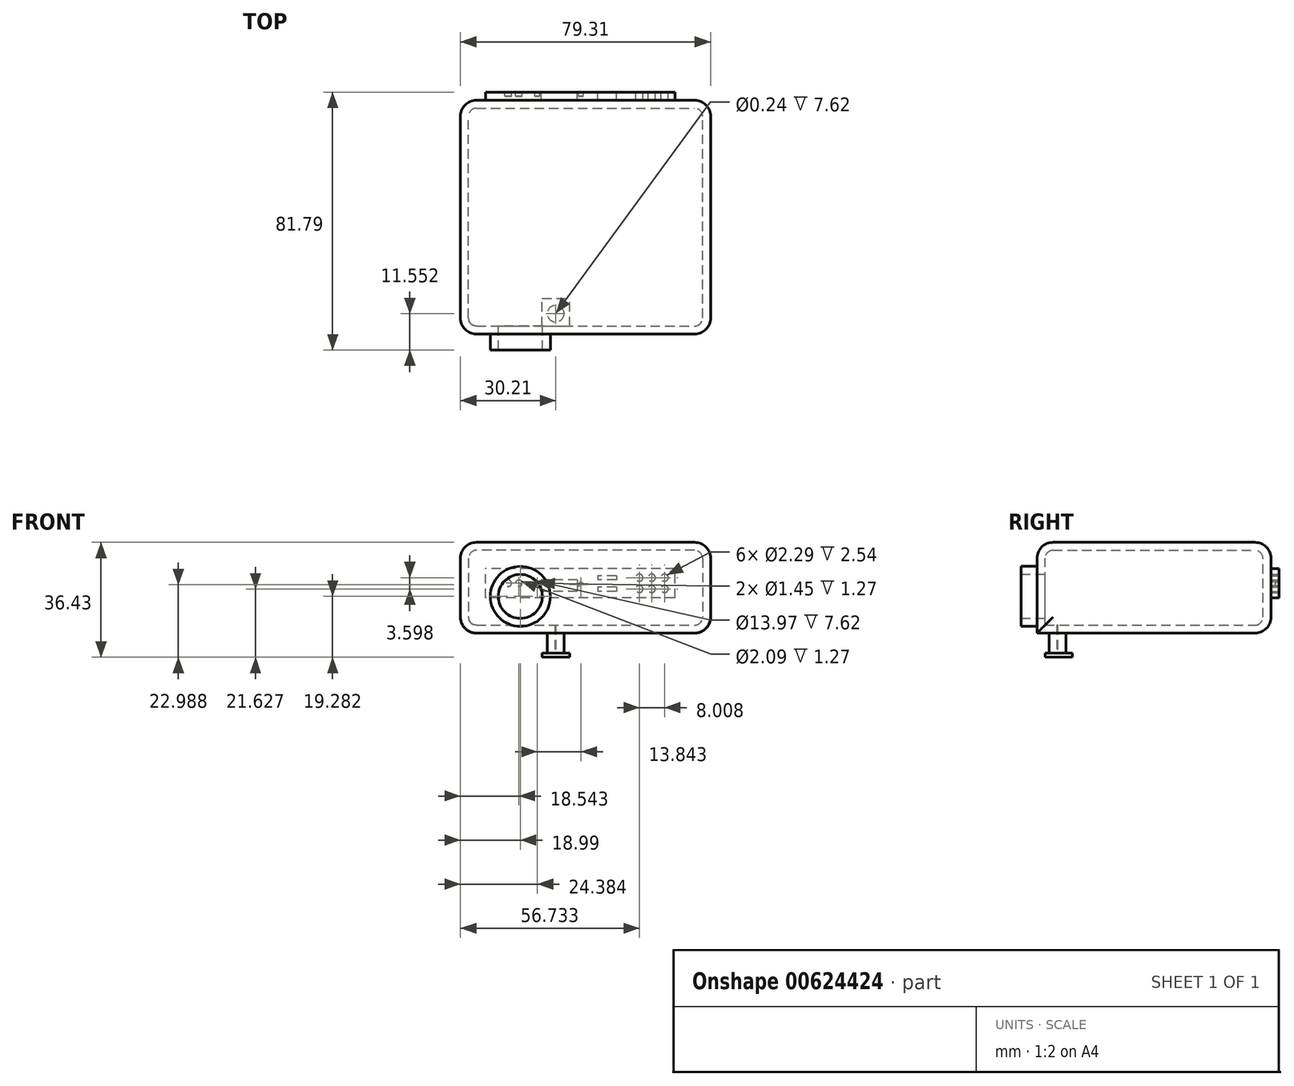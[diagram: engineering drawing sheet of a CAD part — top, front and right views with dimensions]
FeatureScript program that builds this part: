
annotation { "Feature Type Name" : "Feature", "Feature Type Description" : "" }
export const myFeature = defineFeature(function(context is Context, id is Id, definition is map)
    precondition{}
    {
        {
            var Q0;
            Q0=qCreatedBy(makeId("Front.planeOp"),FACE);
            var sketch = newSketch(context, id + "F0", { "sketchPlane" : qUnion([Q0])});
            skLineSegment(sketch, "E0.bottom", {"start": v(0, 0) * mm, "end": v(79.31, 0) * mm});
            skLineSegment(sketch, "E0.top", {"start": v(0, 28.8) * mm, "end": v(79.31, 28.8) * mm});
            skLineSegment(sketch, "E0.left", {"start": v(0, 0) * mm, "end": v(0, 28.8) * mm});
            skLineSegment(sketch, "E0.right", {"start": v(79.31, 0) * mm, "end": v(79.31, 28.8) * mm});
            skSolve(sketch);
        }
        {
            var Q0;
            Q0=makeQuery(id+"F0.imprint","IMPRINT",FACE,{"disambiguationData":[TD([[makeQuery(id+"F0.imprint","IMPRINT",EDGE,{"derivedFrom":sQuery(id+"F0.wireOp",EDGE,"E0.bottom")}),1.0]])]});
            extrude(context, id + "F1", {"entities" : qUnion([Q0]), "oppositeDirection" : true, "depth" : 74.17 * mm, "offsetDistance" : 25.4 * mm});
        }
        {
            var Q0;
            Q0=makeQuery(id+"F1.opExtrude","CAP_FACE",FACE,{"disambiguationData":[OSD([sQuery(id+"F0.wireOp",EDGE,"E0.bottom"),sQuery(id+"F0.wireOp",EDGE,"E0.top"),sQuery(id+"F0.wireOp",EDGE,"E0.left"),sQuery(id+"F0.wireOp",EDGE,"E0.right")])],"isStart":false});
            fillet(context, id + "F2", {"entities" : qUnion([Q0]), "radius" : 5.08 * mm, "tangentPropagation" : true, "allowEdgeOverflow" : false});
        }
        {
            var Q0;
            Q0=makeQuery(id+"F1.opExtrude","SWEPT_FACE",FACE,{"disambiguationData":[OSD([sQuery(id+"F0.wireOp",EDGE,"E0.right")])]});
            fillet(context, id + "F3", {"entities" : qUnion([Q0]), "radius" : 5.08 * mm, "tangentPropagation" : true, "allowEdgeOverflow" : false});
        }
        {
            var Q0;
            Q0=makeQuery(id+"F1.opExtrude","SWEPT_FACE",FACE,{"disambiguationData":[OSD([sQuery(id+"F0.wireOp",EDGE,"E0.bottom")])]});
            var sketch = newSketch(context, id + "F4", { "sketchPlane" : qUnion([Q0])});
            skCircle(sketch, "E1", {"center": v(30.2, -6.47) * mm, "radius": 2.66 * mm});
            skSolve(sketch);
        }
        {
            var Q0;
            Q0 = qSketchRegion(id + "F4", true);
            extrude(context, id + "F5", {"entities" : qUnion([Q0]), "operationType" : NewBodyOperationType.ADD, "depth" : 6.35 * mm, "offsetDistance" : 25.4 * mm});
        }
        {
            var Q0;
            Q0=makeQuery(id+"F5.opExtrude","CAP_FACE",FACE,{"disambiguationData":[OSD([sQuery(id+"F4.wireOp",EDGE,"E1")])],"isStart":false});
            var sketch = newSketch(context, id + "F6", { "sketchPlane" : qUnion([Q0])});
            skLineSegment(sketch, "E2.bottom", {"start": v(25.91, -2.52) * mm, "end": v(34.65, -2.52) * mm});
            skLineSegment(sketch, "E2.top", {"start": v(25.91, -11.26) * mm, "end": v(34.65, -11.26) * mm});
            skLineSegment(sketch, "E2.left", {"start": v(25.91, -2.52) * mm, "end": v(25.91, -11.26) * mm});
            skLineSegment(sketch, "E2.right", {"start": v(34.65, -2.52) * mm, "end": v(34.65, -11.26) * mm});
            skSolve(sketch);
        }
        {
            var Q0;
            Q0 = qSketchRegion(id + "F6", true);
            extrude(context, id + "F7", {"entities" : qUnion([Q0]), "operationType" : NewBodyOperationType.ADD, "depth" : 1.27 * mm, "offsetDistance" : 25.4 * mm});
        }
        {
            var Q0;
            Q0=makeQuery(id+"F1.opExtrude","SWEPT_FACE",FACE,{"disambiguationData":[OSD([sQuery(id+"F0.wireOp",EDGE,"E0.top")])]});
            fillet(context, id + "F8", {"entities" : qUnion([Q0]), "radius" : 5.08 * mm, "tangentPropagation" : true, "allowEdgeOverflow" : false});
        }
        {
            var Q0;
            Q0=makeQuery(id+"F1.opExtrude","SWEPT_FACE",FACE,{"disambiguationData":[OSD([sQuery(id+"F0.wireOp",EDGE,"E0.left")])]});
            fillet(context, id + "F9", {"entities" : qUnion([Q0]), "radius" : 5.08 * mm, "tangentPropagation" : true, "allowEdgeOverflow" : false});
        }
        {
            var Q0;
            Q0=qCreatedBy(makeId("Front.planeOp"),FACE);
            var sketch = newSketch(context, id + "F10", { "sketchPlane" : qUnion([Q0])});
            skCircle(sketch, "E3", {"center": v(18.99, 11.66) * mm, "radius": 9.53 * mm});
            skSolve(sketch);
        }
        {
            var Q0;
            Q0 = qSketchRegion(id + "F10", true);
            extrude(context, id + "F11", {"entities" : qUnion([Q0]), "operationType" : NewBodyOperationType.ADD, "depth" : 5.08 * mm, "offsetDistance" : 25.4 * mm});
        }
        {
            var Q0;
            Q0=makeQuery(id+"F11.opExtrude","CAP_FACE",FACE,{"disambiguationData":[OSD([sQuery(id+"F10.wireOp",EDGE,"E3")])],"isStart":false});
            shell(context, id + "F12", {"entities" : qUnion([Q0]), "thickness" : 2.54 * mm});
        }
        {
            var Q0;
            Q0=makeQuery(id+"F1.opExtrude","CAP_FACE",FACE,{"disambiguationData":[OSD([sQuery(id+"F0.wireOp",EDGE,"E0.bottom"),sQuery(id+"F0.wireOp",EDGE,"E0.top"),sQuery(id+"F0.wireOp",EDGE,"E0.left"),sQuery(id+"F0.wireOp",EDGE,"E0.right")])],"isStart":false});
            var sketch = newSketch(context, id + "F13", { "sketchPlane" : qUnion([Q0])});
            skLineSegment(sketch, "E4.bottom", {"start": v(-68.05, 11.14) * mm, "end": v(-7.92, 11.14) * mm});
            skLineSegment(sketch, "E4.top", {"start": v(-68.05, 20.48) * mm, "end": v(-7.92, 20.48) * mm});
            skLineSegment(sketch, "E4.left", {"start": v(-68.05, 11.14) * mm, "end": v(-68.05, 20.48) * mm});
            skLineSegment(sketch, "E4.right", {"start": v(-7.92, 11.14) * mm, "end": v(-7.92, 20.48) * mm});
            skSolve(sketch);
        }
        {
            var Q0;
            Q0=makeQuery(id+"F13.imprint","IMPRINT",FACE,{"disambiguationData":[TD([[makeQuery(id+"F13.imprint","IMPRINT",EDGE,{"derivedFrom":sQuery(id+"F13.wireOp",EDGE,"E4.bottom")}),1.0]])]});
            extrude(context, id + "F14", {"entities" : qUnion([Q0]), "operationType" : NewBodyOperationType.ADD, "depth" : 2.54 * mm, "offsetDistance" : 25.4 * mm});
        }
        {
            var Q0;
            Q0=makeQuery(id+"F14.opExtrude","CAP_FACE",FACE,{"disambiguationData":[OSD([sQuery(id+"F13.wireOp",EDGE,"E4.bottom"),sQuery(id+"F13.wireOp",EDGE,"E4.top"),sQuery(id+"F13.wireOp",EDGE,"E4.left"),sQuery(id+"F13.wireOp",EDGE,"E4.right")])],"isStart":false});
            var sketch = newSketch(context, id + "F15", { "sketchPlane" : qUnion([Q0])});
            skCircle(sketch, "E5", {"center": v(-64.74, 17.6) * mm, "radius": 1.14 * mm});
            skCircle(sketch, "E6", {"center": v(-60.68, 17.6) * mm, "radius": 1.14 * mm});
            skCircle(sketch, "E7", {"center": v(-56.73, 17.6) * mm, "radius": 1.14 * mm});
            skCircle(sketch, "E8", {"center": v(-64.74, 14) * mm, "radius": 1.14 * mm});
            skCircle(sketch, "E9", {"center": v(-60.68, 14) * mm, "radius": 1.14 * mm});
            skCircle(sketch, "E10", {"center": v(-56.73, 14) * mm, "radius": 1.14 * mm});
            skSolve(sketch);
        }
        {
            var Q0;
            Q0=makeQuery(id+"F15.imprint","IMPRINT",FACE,{"disambiguationData":[TD([[makeQuery(id+"F15.imprint","IMPRINT",EDGE,{"derivedFrom":sQuery(id+"F15.wireOp",EDGE,"E5")}),-1.0]])]});
            var sketch = newSketch(context, id + "F16", { "sketchPlane" : qUnion([Q0])});
            skLineSegment(sketch, "E11.bottom", {"start": v(-49.45, 18.24) * mm, "end": v(-43.59, 18.24) * mm});
            skLineSegment(sketch, "E11.top", {"start": v(-49.45, 16.86) * mm, "end": v(-43.59, 16.86) * mm});
            skLineSegment(sketch, "E11.left", {"start": v(-49.45, 18.24) * mm, "end": v(-49.45, 16.86) * mm});
            skLineSegment(sketch, "E11.right", {"start": v(-43.59, 18.24) * mm, "end": v(-43.59, 16.86) * mm});
            skLineSegment(sketch, "E12.bottom", {"start": v(-49.45, 14.62) * mm, "end": v(-43.59, 14.62) * mm});
            skLineSegment(sketch, "E12.top", {"start": v(-49.45, 13.25) * mm, "end": v(-43.59, 13.25) * mm});
            skLineSegment(sketch, "E12.left", {"start": v(-49.45, 14.62) * mm, "end": v(-49.45, 13.25) * mm});
            skLineSegment(sketch, "E12.right", {"start": v(-43.59, 14.62) * mm, "end": v(-43.59, 13.25) * mm});
            skLineSegment(sketch, "E13.bottom", {"start": v(-37.1, 16.86) * mm, "end": v(-25.63, 16.86) * mm});
            skLineSegment(sketch, "E13.top", {"start": v(-37.1, 13.25) * mm, "end": v(-25.63, 13.25) * mm});
            skLineSegment(sketch, "E13.left", {"start": v(-37.1, 16.86) * mm, "end": v(-37.1, 13.25) * mm});
            skLineSegment(sketch, "E13.right", {"start": v(-25.63, 16.86) * mm, "end": v(-25.63, 13.25) * mm});
            skSolve(sketch);
        }
        {
            var Q0;
            Q0=makeQuery(id+"F15.imprint","IMPRINT",FACE,{"disambiguationData":[TD([[makeQuery(id+"F15.imprint","IMPRINT",EDGE,{"derivedFrom":sQuery(id+"F15.wireOp",EDGE,"E5")}),-1.0]])]});
            var sketch = newSketch(context, id + "F17", { "sketchPlane" : qUnion([Q0])});
            skCircle(sketch, "E14", {"center": v(-24.38, 15.37) * mm, "radius": 0.73 * mm});
            skCircle(sketch, "E15", {"center": v(-38.23, 15.37) * mm, "radius": 0.73 * mm});
            skSolve(sketch);
        }
        {
            var Q0;
            Q0=makeQuery(id+"F15.imprint","IMPRINT",FACE,{"disambiguationData":[TD([[makeQuery(id+"F15.imprint","IMPRINT",EDGE,{"derivedFrom":sQuery(id+"F15.wireOp",EDGE,"E5")}),1.0]])]});
            var Q1;
            Q1=makeQuery(id+"F15.imprint","IMPRINT",FACE,{"disambiguationData":[TD([[makeQuery(id+"F15.imprint","IMPRINT",EDGE,{"derivedFrom":sQuery(id+"F15.wireOp",EDGE,"E6")}),1.0]])]});
            var Q2;
            Q2=makeQuery(id+"F15.imprint","IMPRINT",FACE,{"disambiguationData":[TD([[makeQuery(id+"F15.imprint","IMPRINT",EDGE,{"derivedFrom":sQuery(id+"F15.wireOp",EDGE,"E7")}),1.0]])]});
            var Q3;
            Q3=makeQuery(id+"F15.imprint","IMPRINT",FACE,{"disambiguationData":[TD([[makeQuery(id+"F15.imprint","IMPRINT",EDGE,{"derivedFrom":sQuery(id+"F15.wireOp",EDGE,"E10")}),1.0]])]});
            var Q4;
            Q4=makeQuery(id+"F15.imprint","IMPRINT",FACE,{"disambiguationData":[TD([[makeQuery(id+"F15.imprint","IMPRINT",EDGE,{"derivedFrom":sQuery(id+"F15.wireOp",EDGE,"E9")}),1.0]])]});
            var Q5;
            Q5=makeQuery(id+"F15.imprint","IMPRINT",FACE,{"disambiguationData":[TD([[makeQuery(id+"F15.imprint","IMPRINT",EDGE,{"derivedFrom":sQuery(id+"F15.wireOp",EDGE,"E8")}),1.0]])]});
            extrude(context, id + "F18", {"entities" : qUnion([Q0, Q1, Q2, Q3, Q4, Q5]), "operationType" : NewBodyOperationType.REMOVE, "oppositeDirection" : true, "depth" : 2.54 * mm, "offsetDistance" : 25.4 * mm});
        }
        {
            var Q0;
            Q0=makeQuery(id+"F17.imprint","IMPRINT",FACE,{"disambiguationData":[TD([[makeQuery(id+"F17.imprint","IMPRINT",EDGE,{"derivedFrom":sQuery(id+"F17.wireOp",EDGE,"E15")}),1.0]])]});
            var Q1;
            Q1=makeQuery(id+"F17.imprint","IMPRINT",FACE,{"disambiguationData":[TD([[makeQuery(id+"F17.imprint","IMPRINT",EDGE,{"derivedFrom":sQuery(id+"F17.wireOp",EDGE,"E14")}),1.0]])]});
            extrude(context, id + "F19", {"entities" : qUnion([Q0, Q1]), "operationType" : NewBodyOperationType.REMOVE, "oppositeDirection" : true, "depth" : 1.27 * mm, "offsetDistance" : 25.4 * mm});
        }
        {
            var Q0;
            Q0=makeQuery(id+"F16.imprint","IMPRINT",FACE,{"disambiguationData":[TD([[makeQuery(id+"F16.imprint","IMPRINT",EDGE,{"derivedFrom":sQuery(id+"F16.wireOp",EDGE,"E13.bottom")}),-1.0]])]});
            var Q1;
            Q1=makeQuery(id+"F16.imprint","IMPRINT",FACE,{"disambiguationData":[TD([[makeQuery(id+"F16.imprint","IMPRINT",EDGE,{"derivedFrom":sQuery(id+"F16.wireOp",EDGE,"E11.bottom")}),-1.0]])]});
            var Q2;
            Q2=makeQuery(id+"F16.imprint","IMPRINT",FACE,{"disambiguationData":[TD([[makeQuery(id+"F16.imprint","IMPRINT",EDGE,{"derivedFrom":sQuery(id+"F16.wireOp",EDGE,"E12.bottom")}),-1.0]])]});
            extrude(context, id + "F20", {"entities" : qUnion([Q0, Q1, Q2]), "operationType" : NewBodyOperationType.REMOVE, "oppositeDirection" : true, "depth" : 2.54 * mm, "offsetDistance" : 25.4 * mm});
        }
        {
            var Q0;
            Q0=makeQuery(id+"F14.opExtrude","CAP_FACE",FACE,{"disambiguationData":[OSD([sQuery(id+"F13.wireOp",EDGE,"E4.bottom"),sQuery(id+"F13.wireOp",EDGE,"E4.top"),sQuery(id+"F13.wireOp",EDGE,"E4.left"),sQuery(id+"F13.wireOp",EDGE,"E4.right")])],"isStart":false});
            var sketch = newSketch(context, id + "F21", { "sketchPlane" : qUnion([Q0])});
            skCircle(sketch, "E16", {"center": v(-18.54, 15.85) * mm, "radius": 1.05 * mm});
            skCircle(sketch, "E17", {"center": v(-15.17, 15.85) * mm, "radius": 1.04 * mm});
            skSolve(sketch);
        }
        {
            var Q0;
            Q0=makeQuery(id+"F21.imprint","IMPRINT",FACE,{"disambiguationData":[TD([[makeQuery(id+"F21.imprint","IMPRINT",EDGE,{"derivedFrom":sQuery(id+"F21.wireOp",EDGE,"E16")}),1.0]])]});
            var Q1;
            Q1=makeQuery(id+"F21.imprint","IMPRINT",FACE,{"disambiguationData":[TD([[makeQuery(id+"F21.imprint","IMPRINT",EDGE,{"derivedFrom":sQuery(id+"F21.wireOp",EDGE,"E17")}),1.0]])]});
            extrude(context, id + "F22", {"entities" : qUnion([Q0, Q1]), "operationType" : NewBodyOperationType.REMOVE, "oppositeDirection" : true, "depth" : 1.27 * mm, "offsetDistance" : 25.4 * mm});
        }
    });
